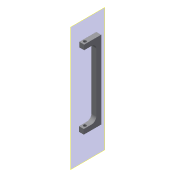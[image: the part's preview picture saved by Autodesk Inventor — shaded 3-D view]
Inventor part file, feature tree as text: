
AUTODESK INVENTOR PART (.ipt)
format: ipt  version: 2019.4 (Build 234330000, 330)  size: 114,688 bytes
history: native  units: mm
features: other x10, reference x6, sketch x3, plane x2, extrude x2, hole x1, projected_geometry x1
ambient origin geometry x8: Origin, YZ Plane, XZ Plane, XY Plane, X Axis, Y Axis, Z Axis, Center Point
bodies: Solid1 (feature_tree)
feature tree (25):
  plane  "Work Plane1"
  sketch  "Sketch1"  dims[d0=10.0mm d1=10.0mm]
  plane  "Work Plane2"
  extrude  "Extrusion1"  Depth=10.0mm
  extrude  "Extrusion2"  Depth=10.0mm
  hole  "Hole1"  [1 undecoded]
  reference  "Reference1"
  reference  "Reference2"
  reference  "Reference3"
  sketch  "Sketch2"  dims[d2=42.0mm d3=10.0mm]
  projected_geometry  "Projected Loop1"
  sketch  "Sketch3"  dims[d4=140.0mm d5=10.0mm d6=10.0mm d7=0.0mm d8=6.0mm d9=10.0mm d10=0.0mm d11=2.9mm d12=6.0mm d13=4.0mm d14=2.0mm d15=90.0deg d16=8.0mm d17=20.594885mm d18=0.0mm d19=6.0mm]
  reference  "Reference4"
  reference  "Reference5"
  reference  "Reference6"
  other  "Assembly_Opentrons_Imagingunit_v1.iam"
  other  "Assembly_opentrons_microscope_slide_y_base:1"
  other  "02_Opentrons_Microscope_Base_v0:1"
  other  "Assembly_opentrons_microscope_slide_y:1"
  other  "Assembly_spindeldrive_350mm:1"
  other  "00_spindel_350mm:1"
  other  "Assembly_Opentrons_Autofocus_v1:1"
  other  "01_Slide_camera_x_rail:1"
  other  "04_OPENTRONS_Microscope_wellplate_base:1"
  other  "09_Opentrons_Microscope_Baseplate:1"
note: 1 required parameter value undecoded (feature->parameter linkage not recoverable at this tier; creation-order binding heuristic only, values carry confidence <= 0.55)
